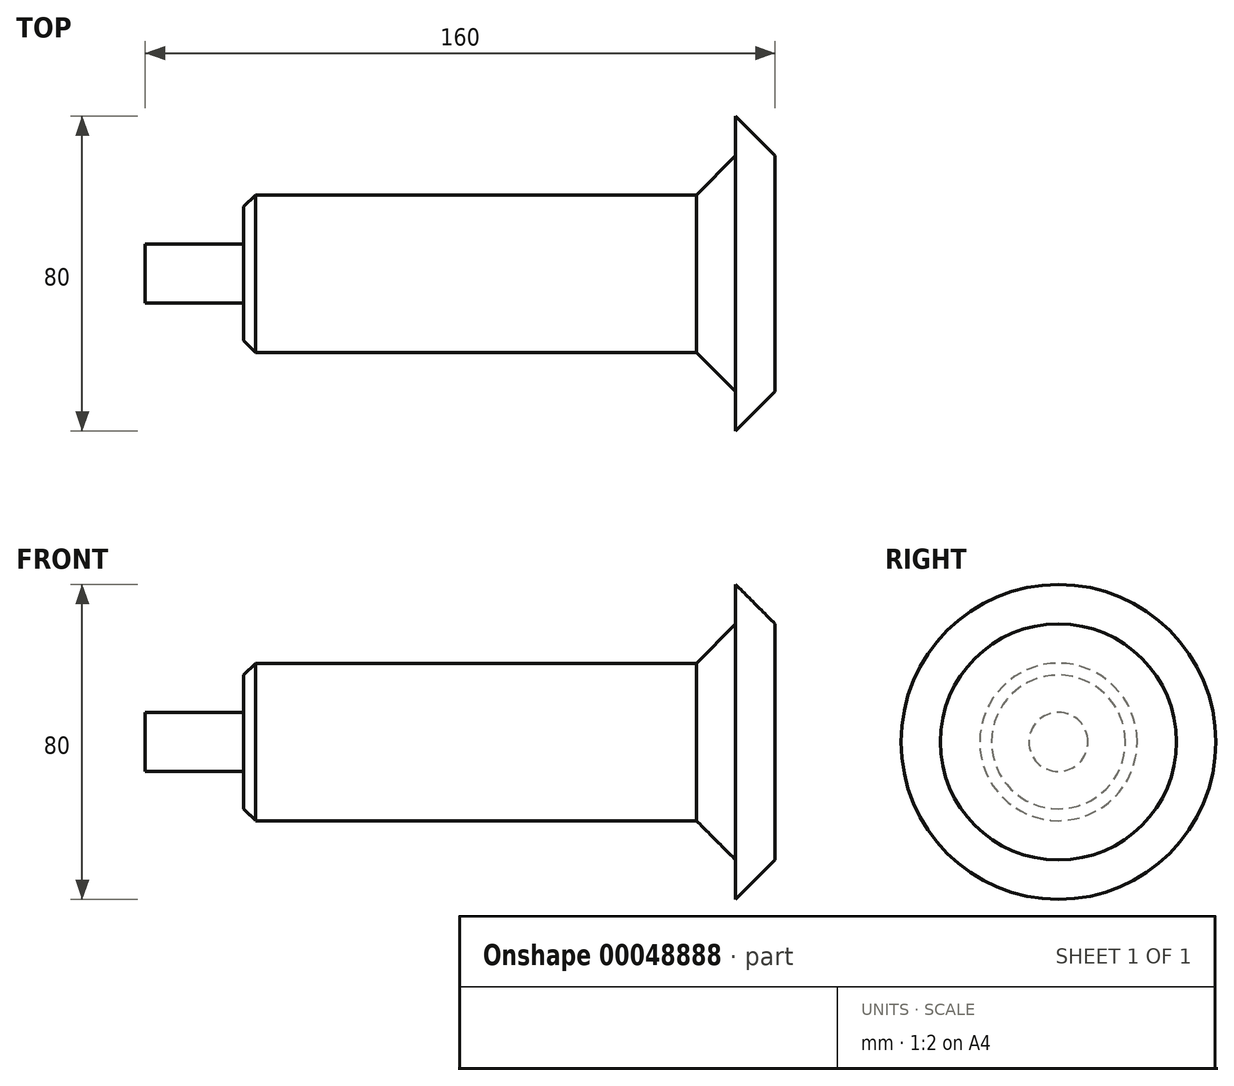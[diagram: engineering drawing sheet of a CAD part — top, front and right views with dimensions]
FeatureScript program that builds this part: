
annotation { "Feature Type Name" : "Feature", "Feature Type Description" : "" }
export const myFeature = defineFeature(function(context is Context, id is Id, definition is map)
    precondition{}
    {
        {
            var Q0;
            Q0=qCreatedBy(makeId("Top.planeOp"),FACE);
            var sketch = newSketch(context, id + "F0", { "sketchPlane" : qUnion([Q0])});
            skLineSegment(sketch, "E0", {"start": v(0, 0) * mm, "end": v(0, -7.5) * mm});
            skLineSegment(sketch, "E1", {"start": v(0, -7.5) * mm, "end": v(25, -7.5) * mm});
            skLineSegment(sketch, "E2", {"start": v(25, -7.5) * mm, "end": v(25, -20) * mm});
            skLineSegment(sketch, "E3", {"start": v(25, -20) * mm, "end": v(150, -20) * mm});
            skLineSegment(sketch, "E4", {"start": v(150, -20) * mm, "end": v(150, -40) * mm});
            skLineSegment(sketch, "E5", {"start": v(150, -40) * mm, "end": v(160, -40) * mm});
            skLineSegment(sketch, "E6", {"start": v(160, -40) * mm, "end": v(160, 0) * mm});
            skLineSegment(sketch, "E7", {"start": v(160, 0) * mm, "end": v(0, 0) * mm});
            skSolve(sketch);
        }
        {
            var Q0;
            Q0=makeQuery(id+"F0.imprint","IMPRINT",FACE,{"disambiguationData":[TD([[makeQuery(id+"F0.imprint","IMPRINT",EDGE,{"derivedFrom":sQuery(id+"F0.wireOp",EDGE,"E0")}),1.0]])]});
            var Q1;
            Q1=sQuery(id+"F0.wireOp",EDGE,"E7");
            revolve(context, id + "F1", {"entities" : qUnion([Q0]), "axis" : qUnion([Q1]), "revolveType" : RevolveType.FULL});
        }
        {
            var Q0;
            Q0=makeQuery(id+"F1.opRevolve","SWEPT_EDGE",EDGE,{"disambiguationData":[OSD([sQuery(id+"F0.wireOp",EDGE,"E2"),sQuery(id+"F0.wireOp",EDGE,"E3")])]});
            chamfer(context, id + "F2", {"entities" : qUnion([Q0]), "chamferType" : ChamferType.OFFSET_ANGLE, "width" : 3 * mm, "oppositeDirection" : false, "angle" : 45 * degree, "tangentPropagation" : true});
        }
        {
            var Q0;
            Q0=makeQuery(id+"F1.opRevolve","SWEPT_EDGE",EDGE,{"disambiguationData":[OSD([sQuery(id+"F0.wireOp",EDGE,"E3"),sQuery(id+"F0.wireOp",EDGE,"E4")])]});
            chamfer(context, id + "F3", {"entities" : qUnion([Q0]), "chamferType" : ChamferType.OFFSET_ANGLE, "width" : 10 * mm, "oppositeDirection" : false, "angle" : 45 * degree, "tangentPropagation" : true});
        }
        {
            var Q0;
            Q0=makeQuery(id+"F1.opRevolve","SWEPT_EDGE",EDGE,{"disambiguationData":[OSD([sQuery(id+"F0.wireOp",EDGE,"E5"),sQuery(id+"F0.wireOp",EDGE,"E6")])]});
            chamfer(context, id + "F4", {"entities" : qUnion([Q0]), "chamferType" : ChamferType.OFFSET_ANGLE, "width" : 10 * mm, "oppositeDirection" : false, "angle" : 45 * degree, "tangentPropagation" : true});
        }
    });
